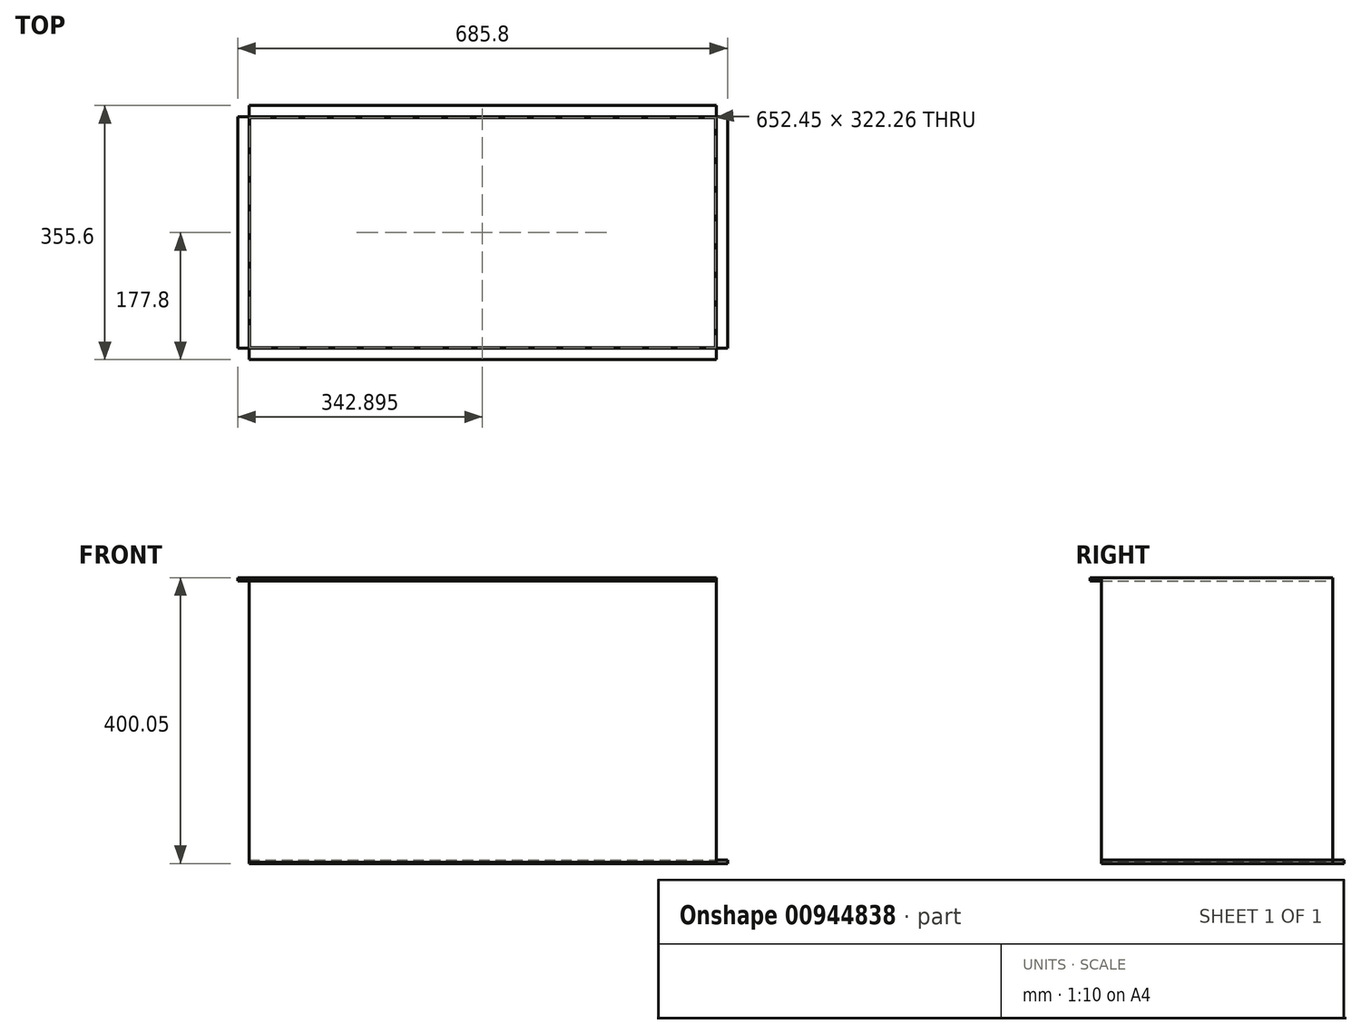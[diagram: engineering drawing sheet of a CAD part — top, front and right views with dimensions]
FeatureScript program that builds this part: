
annotation { "Feature Type Name" : "Feature", "Feature Type Description" : "" }
export const myFeature = defineFeature(function(context is Context, id is Id, definition is map)
    precondition{}
    {
        {
            var Q0;
            Q0=qCreatedBy(makeId("Top.planeOp"),FACE);
            var sketch = newSketch(context, id + "F0", { "sketchPlane" : qUnion([Q0])});
            skLineSegment(sketch, "E0.bottom", {"start": v(-325.37, -177.5) * mm, "end": v(328.68, -177.5) * mm});
            skLineSegment(sketch, "E0.top", {"start": v(-325.37, 146.34) * mm, "end": v(328.68, 146.34) * mm});
            skLineSegment(sketch, "E0.left", {"start": v(-325.37, -177.5) * mm, "end": v(-325.37, 146.34) * mm});
            skLineSegment(sketch, "E0.right", {"start": v(328.68, -177.5) * mm, "end": v(328.68, 146.34) * mm});
            skLineSegment(sketch, "E1.top", {"start": v(-341.25, 146.34) * mm, "end": v(-325.37, 146.34) * mm});
            skLineSegment(sketch, "E1.right", {"start": v(-325.37, 162.22) * mm, "end": v(-325.37, 146.34) * mm});
            skLineSegment(sketch, "E2", {"start": v(-325.37, -177.5) * mm, "end": v(-341.25, -177.5) * mm});
            skLineSegment(sketch, "E3", {"start": v(-341.25, 146.34) * mm, "end": v(-341.25, -177.5) * mm});
            skLineSegment(sketch, "E4", {"start": v(328.68, 146.34) * mm, "end": v(328.68, 162.22) * mm});
            skLineSegment(sketch, "E5", {"start": v(328.68, 146.34) * mm, "end": v(344.55, 146.34) * mm});
            skLineSegment(sketch, "E6", {"start": v(-325.37, 162.22) * mm, "end": v(328.68, 162.22) * mm});
            skLineSegment(sketch, "E7", {"start": v(-325.37, -177.5) * mm, "end": v(-325.37, -193.38) * mm});
            skLineSegment(sketch, "E8", {"start": v(328.68, -177.5) * mm, "end": v(328.68, -193.38) * mm});
            skLineSegment(sketch, "E9", {"start": v(-325.37, -193.38) * mm, "end": v(328.68, -193.38) * mm});
            skLineSegment(sketch, "E10", {"start": v(328.68, -177.5) * mm, "end": v(344.55, -177.5) * mm});
            skLineSegment(sketch, "E11", {"start": v(344.55, 146.34) * mm, "end": v(344.55, -177.5) * mm});
            skLineSegment(sketch, "E12.bottom", {"start": v(-324.58, 145.55) * mm, "end": v(327.87, 145.55) * mm});
            skLineSegment(sketch, "E12.top", {"start": v(-324.58, -176.71) * mm, "end": v(327.87, -176.71) * mm});
            skLineSegment(sketch, "E12.left", {"start": v(-324.58, 145.55) * mm, "end": v(-324.58, -176.71) * mm});
            skLineSegment(sketch, "E12.right", {"start": v(327.87, 145.55) * mm, "end": v(327.87, -176.71) * mm});
            skPoint(sketch, "E13", {"position": v(-324.58, -176.71) * mm});
            skLineSegment(sketch, "E14.bottom", {"start": v(328.68, 146.34) * mm, "end": v(330.27, 146.34) * mm});
            skLineSegment(sketch, "E14.top", {"start": v(328.68, 147.93) * mm, "end": v(330.27, 147.93) * mm});
            skLineSegment(sketch, "E14.left", {"start": v(328.68, 146.34) * mm, "end": v(328.68, 147.93) * mm});
            skLineSegment(sketch, "E14.right", {"start": v(330.27, 146.34) * mm, "end": v(330.27, 147.93) * mm});
            skLineSegment(sketch, "E15.bottom", {"start": v(328.68, -177.5) * mm, "end": v(328.68, -179.1) * mm});
            skLineSegment(sketch, "E15.top", {"start": v(330.27, -177.5) * mm, "end": v(330.27, -179.1) * mm});
            skLineSegment(sketch, "E15.left", {"start": v(328.68, -177.5) * mm, "end": v(330.27, -177.5) * mm});
            skLineSegment(sketch, "E15.right", {"start": v(328.68, -179.1) * mm, "end": v(330.27, -179.1) * mm});
            skLineSegment(sketch, "E16.bottom", {"start": v(-326.96, -179.1) * mm, "end": v(-325.37, -179.1) * mm});
            skLineSegment(sketch, "E16.top", {"start": v(-326.96, -177.5) * mm, "end": v(-325.37, -177.5) * mm});
            skLineSegment(sketch, "E16.left", {"start": v(-326.96, -179.1) * mm, "end": v(-326.96, -177.5) * mm});
            skLineSegment(sketch, "E16.right", {"start": v(-325.37, -179.1) * mm, "end": v(-325.37, -177.5) * mm});
            skLineSegment(sketch, "E17.bottom", {"start": v(-326.96, 146.34) * mm, "end": v(-325.37, 146.34) * mm});
            skLineSegment(sketch, "E17.top", {"start": v(-326.96, 147.93) * mm, "end": v(-325.37, 147.93) * mm});
            skLineSegment(sketch, "E17.left", {"start": v(-326.96, 146.34) * mm, "end": v(-326.96, 147.93) * mm});
            skLineSegment(sketch, "E17.right", {"start": v(-325.37, 146.34) * mm, "end": v(-325.37, 147.93) * mm});
            skSolve(sketch);
        }
        {
            var Q0;
            Q0=makeQuery(id+"F0.imprint","IMPRINT",FACE,{"disambiguationData":[TD([[makeQuery(id+"F0.imprint","IMPRINT",EDGE,{"derivedFrom":sQuery(id+"F0.wireOp",EDGE,"E0.bottom")}),1.0]])]});
            extrude(context, id + "F1", {"entities" : qUnion([Q0]), "depth" : 400.05 * mm, "offsetDistance" : 25.4 * mm});
        }
        {
            var Q0;
            Q0=makeQuery(id+"F0.imprint","IMPRINT",FACE,{"disambiguationData":[TD([[makeQuery(id+"F0.imprint","IMPRINT",EDGE,{"derivedFrom":sQuery(id+"F0.wireOp",EDGE,"E0.bottom")}),1.0]])]});
            var Q1;
            Q1=makeQuery(id+"F0.imprint","IMPRINT",FACE,{"disambiguationData":[TD([[makeQuery(id+"F0.imprint","IMPRINT",EDGE,{"derivedFrom":sQuery(id+"F0.wireOp",EDGE,"E12.bottom")}),-1.0]])]});
            extrude(context, id + "F2", {"entities" : qUnion([Q0, Q1]), "depth" : 1.59 * mm, "offsetDistance" : 25.4 * mm});
        }
        {
            var Q0;
            Q0=makeQuery(id+"F0.imprint","IMPRINT",FACE,{"disambiguationData":[TD([[makeQuery(id+"F0.imprint","IMPRINT",EDGE,{"derivedFrom":sQuery(id+"F0.wireOp",EDGE,"E0.top")}),1.0]])]});
            var Q1;
            Q1=makeQuery(id+"F0.imprint","IMPRINT",FACE,{"disambiguationData":[TD([[makeQuery(id+"F0.imprint","IMPRINT",EDGE,{"derivedFrom":sQuery(id+"F0.wireOp",EDGE,"E0.right")}),-1.0]])]});
            var Q2;
            Q2=makeQuery(id+"F0.imprint","IMPRINT",FACE,{"disambiguationData":[TD([[makeQuery(id+"F0.imprint","IMPRINT",EDGE,{"derivedFrom":sQuery(id+"F0.wireOp",EDGE,"E14.bottom")}),1.0]])]});
            var Q3;
            Q3=makeQuery(id+"F0.imprint","IMPRINT",FACE,{"disambiguationData":[TD([[makeQuery(id+"F0.imprint","IMPRINT",EDGE,{"derivedFrom":sQuery(id+"F0.wireOp",EDGE,"E0.bottom")}),-1.0]])]});
            var Q4;
            Q4=makeQuery(id+"F0.imprint","IMPRINT",FACE,{"disambiguationData":[TD([[makeQuery(id+"F0.imprint","IMPRINT",EDGE,{"derivedFrom":sQuery(id+"F0.wireOp",EDGE,"E15.bottom")}),1.0]])]});
            var Q5;
            Q5=makeQuery(id+"F0.imprint","IMPRINT",FACE,{"disambiguationData":[TD([[makeQuery(id+"F0.imprint","IMPRINT",EDGE,{"derivedFrom":sQuery(id+"F0.wireOp",EDGE,"E16.bottom")}),1.0]])]});
            var Q6;
            Q6=makeQuery(id+"F0.imprint","IMPRINT",FACE,{"disambiguationData":[TD([[makeQuery(id+"F0.imprint","IMPRINT",EDGE,{"derivedFrom":sQuery(id+"F0.wireOp",EDGE,"E0.left")}),1.0]])]});
            var Q7;
            Q7=makeQuery(id+"F0.imprint","IMPRINT",FACE,{"disambiguationData":[TD([[makeQuery(id+"F0.imprint","IMPRINT",EDGE,{"derivedFrom":sQuery(id+"F0.wireOp",EDGE,"E17.bottom")}),1.0]])]});
            extrude(context, id + "F3", {"entities" : qUnion([Q0, Q1, Q2, Q3, Q4, Q5, Q6, Q7]), "depth" : 4.78 * mm, "offsetDistance" : 25.4 * mm});
        }
        {
            var Q0;
            Q0=makeQuery(id+"F3.opExtrude","SWEPT_BODY",BODY,{"disambiguationData":[OSD([sQuery(id+"F0.wireOp",EDGE,"E0.bottom"),sQuery(id+"F0.wireOp",EDGE,"E0.top"),sQuery(id+"F0.wireOp",EDGE,"E0.left"),sQuery(id+"F0.wireOp",EDGE,"E0.right"),sQuery(id+"F0.wireOp",EDGE,"E1.top"),sQuery(id+"F0.wireOp",EDGE,"E1.right"),sQuery(id+"F0.wireOp",EDGE,"E2"),sQuery(id+"F0.wireOp",EDGE,"E3"),sQuery(id+"F0.wireOp",EDGE,"E4"),sQuery(id+"F0.wireOp",EDGE,"E5"),sQuery(id+"F0.wireOp",EDGE,"E6"),sQuery(id+"F0.wireOp",EDGE,"E7"),sQuery(id+"F0.wireOp",EDGE,"E8"),sQuery(id+"F0.wireOp",EDGE,"E9"),sQuery(id+"F0.wireOp",EDGE,"E10"),sQuery(id+"F0.wireOp",EDGE,"E11"),sQuery(id+"F0.wireOp",EDGE,"E14.top"),sQuery(id+"F0.wireOp",EDGE,"E14.right"),sQuery(id+"F0.wireOp",EDGE,"E15.top"),sQuery(id+"F0.wireOp",EDGE,"E15.right"),sQuery(id+"F0.wireOp",EDGE,"E16.bottom"),sQuery(id+"F0.wireOp",EDGE,"E16.left"),sQuery(id+"F0.wireOp",EDGE,"E17.top"),sQuery(id+"F0.wireOp",EDGE,"E17.left")])]});
            transform(context, id + "F4", {"entities" : qUnion([Q0]), "transformType" : TransformType.TRANSLATION_3D, "dx" : 0 * mm, "dy" : 0 * mm, "dz" : 400.05 * mm, "makeCopy" : false});
        }
        {
            var Q0;
            Q0=makeQuery(id+"F3.opExtrude","SWEPT_BODY",BODY,{"disambiguationData":[OSD([sQuery(id+"F0.wireOp",EDGE,"E0.bottom"),sQuery(id+"F0.wireOp",EDGE,"E0.top"),sQuery(id+"F0.wireOp",EDGE,"E0.left"),sQuery(id+"F0.wireOp",EDGE,"E0.right"),sQuery(id+"F0.wireOp",EDGE,"E1.top"),sQuery(id+"F0.wireOp",EDGE,"E1.right"),sQuery(id+"F0.wireOp",EDGE,"E2"),sQuery(id+"F0.wireOp",EDGE,"E3"),sQuery(id+"F0.wireOp",EDGE,"E4"),sQuery(id+"F0.wireOp",EDGE,"E5"),sQuery(id+"F0.wireOp",EDGE,"E6"),sQuery(id+"F0.wireOp",EDGE,"E7"),sQuery(id+"F0.wireOp",EDGE,"E8"),sQuery(id+"F0.wireOp",EDGE,"E9"),sQuery(id+"F0.wireOp",EDGE,"E10"),sQuery(id+"F0.wireOp",EDGE,"E11"),sQuery(id+"F0.wireOp",EDGE,"E14.top"),sQuery(id+"F0.wireOp",EDGE,"E14.right"),sQuery(id+"F0.wireOp",EDGE,"E15.top"),sQuery(id+"F0.wireOp",EDGE,"E15.right"),sQuery(id+"F0.wireOp",EDGE,"E16.bottom"),sQuery(id+"F0.wireOp",EDGE,"E16.left"),sQuery(id+"F0.wireOp",EDGE,"E17.top"),sQuery(id+"F0.wireOp",EDGE,"E17.left")])]});
            transform(context, id + "F5", {"entities" : qUnion([Q0]), "transformType" : TransformType.TRANSLATION_3D, "dx" : 0 * mm, "dy" : 0 * mm, "dz" : -4.78 * mm, "makeCopy" : false});
        }
    });
